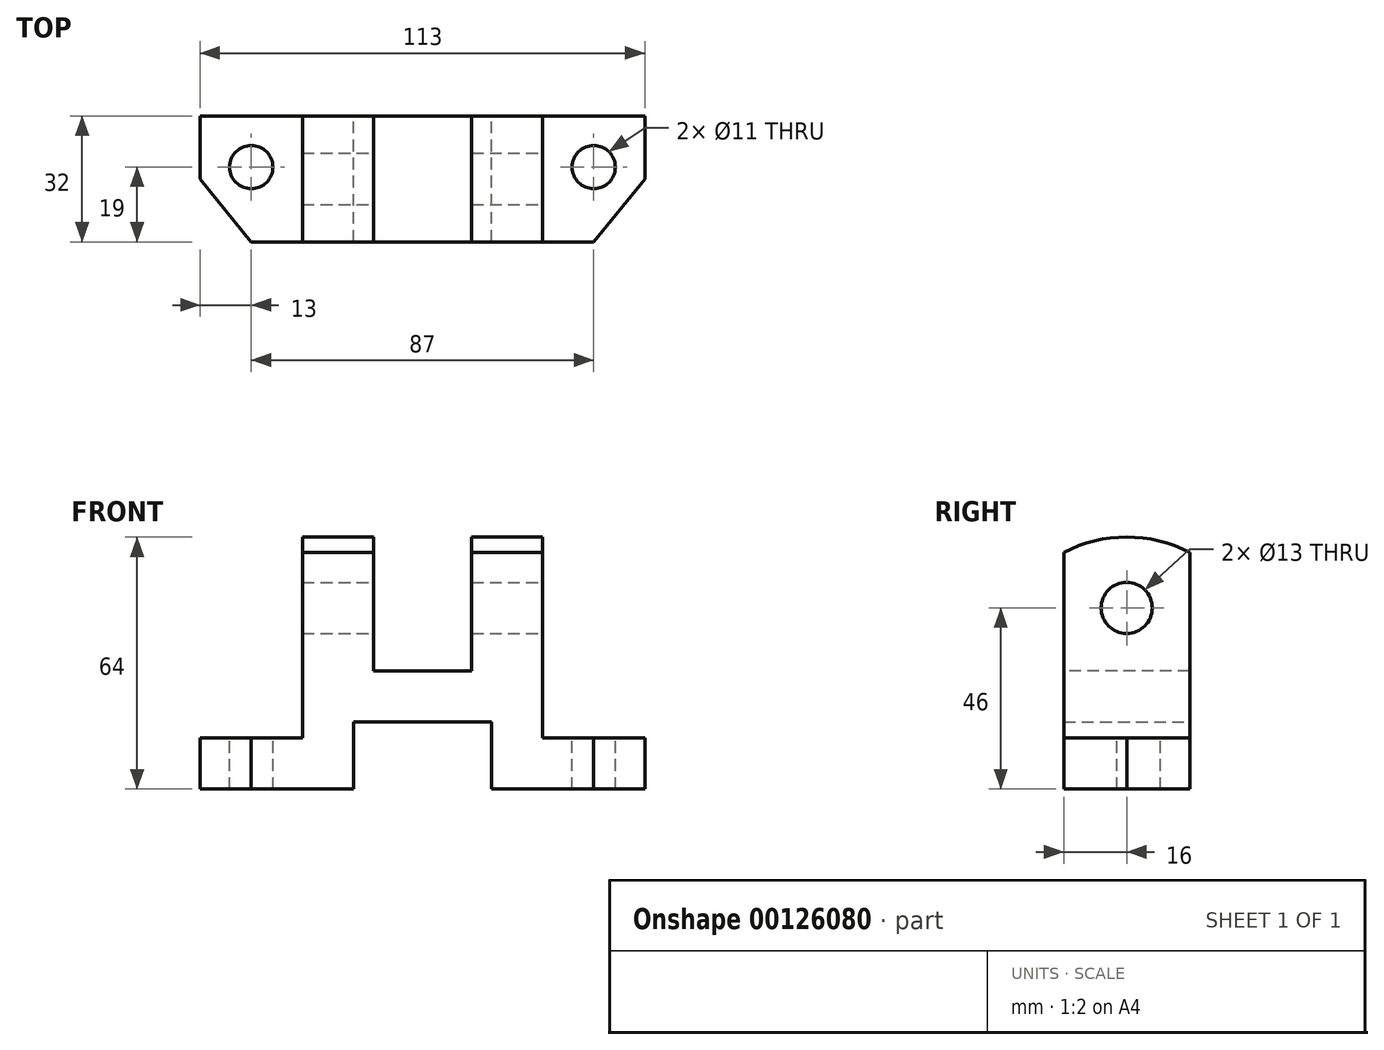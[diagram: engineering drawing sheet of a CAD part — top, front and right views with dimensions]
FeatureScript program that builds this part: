
annotation { "Feature Type Name" : "Feature", "Feature Type Description" : "" }
export const myFeature = defineFeature(function(context is Context, id is Id, definition is map)
    precondition{}
    {
        {
            var Q0;
            Q0=qCreatedBy(makeId("Right.planeOp"),FACE);
            var sketch = newSketch(context, id + "F0", { "sketchPlane" : qUnion([Q0])});
            skLineSegment(sketch, "E0.bottom", {"start": v(0, 0) * mm, "end": v(32, 0) * mm});
            skLineSegment(sketch, "E0.top", {"start": v(0, 13) * mm, "end": v(32, 13) * mm});
            skLineSegment(sketch, "E0.left", {"start": v(0, 0) * mm, "end": v(0, 13) * mm});
            skLineSegment(sketch, "E0.right", {"start": v(32, 0) * mm, "end": v(32, 13) * mm});
            skLineSegment(sketch, "E1", {"start": v(0, 13) * mm, "end": v(0, 60.13) * mm});
            skLineSegment(sketch, "E2", {"start": v(32, 13) * mm, "end": v(32, 60.13) * mm});
            skArc(sketch, "E3", {"start": v(32, 60.13) * mm, "mid": v(16, 64) * mm, "end": v(0, 60.13) * mm});
            skPoint(sketch, "E4", {"position": v(16, 64) * mm});
            skSolve(sketch);
        }
        {
            var Q0;
            Q0 = qSketchRegion(id + "F0", true);
            extrude(context, id + "F1", {"entities" : qUnion([Q0]), "depth" : 113 * mm});
        }
        {
            var Q0;
            Q0=makeQuery(id+"F1.opExtrude","SWEPT_FACE",FACE,{"disambiguationData":[OSD([sQuery(id+"F0.wireOp",EDGE,"E0.bottom")])]});
            var sketch = newSketch(context, id + "F2", { "sketchPlane" : qUnion([Q0])});
            skLineSegment(sketch, "E5.bottom", {"start": v(39, 0) * mm, "end": v(74, 0) * mm});
            skLineSegment(sketch, "E5.top", {"start": v(39, -32) * mm, "end": v(74, -32) * mm});
            skLineSegment(sketch, "E5.left", {"start": v(39, 0) * mm, "end": v(39, -32) * mm});
            skLineSegment(sketch, "E5.right", {"start": v(74, 0) * mm, "end": v(74, -32) * mm});
            skSolve(sketch);
        }
        {
            var Q0;
            Q0=makeQuery(id+"F2.imprint","IMPRINT",FACE,{"disambiguationData":[TD([[makeQuery(id+"F2.imprint","IMPRINT",EDGE,{"derivedFrom":sQuery(id+"F2.wireOp",EDGE,"E5.bottom")}),1.0]])]});
            extrude(context, id + "F3", {"entities" : qUnion([Q0]), "operationType" : NewBodyOperationType.REMOVE, "oppositeDirection" : true, "depth" : 17 * mm});
        }
        {
            var Q0;
            Q0=makeQuery(id+"F1.opExtrude","SWEPT_FACE",FACE,{"disambiguationData":[OSD([sQuery(id+"F0.wireOp",EDGE,"E0.left"),sQuery(id+"F0.wireOp",EDGE,"E1")])]});
            var sketch = newSketch(context, id + "F4", { "sketchPlane" : qUnion([Q0])});
            skLineSegment(sketch, "E6", {"start": v(113, 0) * mm, "end": v(113, 13) * mm});
            skLineSegment(sketch, "E7", {"start": v(113, 13) * mm, "end": v(87, 13) * mm});
            skLineSegment(sketch, "E8", {"start": v(87, 13) * mm, "end": v(87, 78.94) * mm});
            skLineSegment(sketch, "E9", {"start": v(87, 78.94) * mm, "end": v(74, 78.94) * mm});
            skLineSegment(sketch, "E10", {"start": v(69, 30) * mm, "end": v(44, 30) * mm});
            skLineSegment(sketch, "E11", {"start": v(44, 30) * mm, "end": v(44, 78.94) * mm});
            skLineSegment(sketch, "E12", {"start": v(44, 78.94) * mm, "end": v(26, 78.94) * mm});
            skLineSegment(sketch, "E13", {"start": v(26, 78.94) * mm, "end": v(26, 13) * mm});
            skLineSegment(sketch, "E14", {"start": v(0, 13) * mm, "end": v(0, 0) * mm});
            skLineSegment(sketch, "E15", {"start": v(44, 78.94) * mm, "end": v(74, 78.94) * mm});
            skLineSegment(sketch, "E16", {"start": v(87, 78.94) * mm, "end": v(113, 78.94) * mm});
            skLineSegment(sketch, "E17", {"start": v(113, 78.94) * mm, "end": v(113, 13) * mm});
            skLineSegment(sketch, "E18", {"start": v(26, 78.94) * mm, "end": v(0, 78.94) * mm});
            skLineSegment(sketch, "E19", {"start": v(0, 78.94) * mm, "end": v(0, 13) * mm});
            skPoint(sketch, "E20", {"position": v(56.5, 30) * mm});
            skPoint(sketch, "E21", {"position": v(56.5, 17) * mm});
            skLineSegment(sketch, "E22", {"start": v(56.5, 30) * mm, "end": v(56.5, 17) * mm, "construction": true});
            skLineSegment(sketch, "E23", {"start": v(26, 13) * mm, "end": v(0, 13) * mm});
            skLineSegment(sketch, "E24", {"start": v(69, 30) * mm, "end": v(69, 78.94) * mm});
            skSolve(sketch);
        }
        {
            var Q0;
            {var subQ0=sQuery(id+"F4.wireOp",EDGE,"E10");Q0=makeQuery(id+"F4.imprint","IMPRINT",FACE,{"disambiguationData":[TD([[makeQuery(id+"F4.imprint","IMPRINT",EDGE,{"derivedFrom":subQ0}),-1.0]])]});}
            var Q1;
            {var subQ0=sQuery(id+"F4.wireOp",EDGE,"E15");var subQ5=sQuery(id+"F4.wireOp",EDGE,"E24");var subQ6=makeQuery(id+"F4.imprint","INTERSECT",VERTEX,{"derivedFrom":[subQ0,subQ5]});Q1=makeQuery(id+"F4.imprint","IMPRINT",FACE,{"disambiguationData":[TD([[makeQuery(id+"F4.imprint","IMPRINT",EDGE,{"disambiguationData":[TD([[subQ6,1.0]])],"derivedFrom":subQ0}),-1.0]])]});}
            var Q2;
            {var subQ0=sQuery(id+"F4.wireOp",EDGE,"E7");Q2=makeQuery(id+"F4.imprint","IMPRINT",FACE,{"disambiguationData":[TD([[makeQuery(id+"F4.imprint","IMPRINT",EDGE,{"derivedFrom":subQ0}),-1.0]])]});}
            var Q3;
            {var subQ0=sQuery(id+"F4.wireOp",EDGE,"E16");Q3=makeQuery(id+"F4.imprint","IMPRINT",FACE,{"disambiguationData":[TD([[makeQuery(id+"F4.imprint","IMPRINT",EDGE,{"derivedFrom":subQ0}),-1.0]])]});}
            var Q4;
            {var subQ0=sQuery(id+"F4.wireOp",EDGE,"E18");Q4=makeQuery(id+"F4.imprint","IMPRINT",FACE,{"disambiguationData":[TD([[makeQuery(id+"F4.imprint","IMPRINT",EDGE,{"derivedFrom":subQ0}),1.0]])]});}
            var Q5;
            {var subQ0=sQuery(id+"F4.wireOp",EDGE,"E23");Q5=makeQuery(id+"F4.imprint","IMPRINT",FACE,{"disambiguationData":[TD([[makeQuery(id+"F4.imprint","IMPRINT",EDGE,{"derivedFrom":subQ0}),-1.0]])]});}
            extrude(context, id + "F5", {"entities" : qUnion([Q0, Q1, Q2, Q3, Q4, Q5]), "operationType" : NewBodyOperationType.REMOVE, "endBound" : BoundingType.THROUGH_ALL, "oppositeDirection" : true, "depth" : 25 * mm});
        }
        {
            var Q0;
            Q0=makeQuery(id+"F5.boolean.opBoolean","COPY",FACE,{"derivedFrom":makeQuery(id+"F5.opExtrude","SWEPT_FACE",FACE,{"disambiguationData":[OSD([sQuery(id+"F4.wireOp",EDGE,"E7")])]})});
            var sketch = newSketch(context, id + "F6", { "sketchPlane" : qUnion([Q0])});
            skLineSegment(sketch, "E25.bottom", {"start": v(87, 32) * mm, "end": v(113, 32) * mm});
            skLineSegment(sketch, "E25.top", {"start": v(87, 0) * mm, "end": v(100, 0) * mm});
            skLineSegment(sketch, "E25.left", {"start": v(87, 32) * mm, "end": v(87, 0) * mm});
            skLineSegment(sketch, "E25.right", {"start": v(113, 32) * mm, "end": v(113, 16) * mm});
            skLineSegment(sketch, "E26", {"start": v(100, 0) * mm, "end": v(113, 16) * mm});
            skCircle(sketch, "E27", {"center": v(100, 19) * mm, "radius": 5.5 * mm});
            skPoint(sketch, "E27.centerSnap0", {"position": v(100, 32) * mm});
            skSolve(sketch);
        }
        {
            var Q0;
            {var subQ0=sQuery(id+"F6.wireOp",EDGE,"E26");Q0=makeQuery(id+"F6.imprint","IMPRINT",FACE,{"disambiguationData":[TD([[makeQuery(id+"F6.imprint","IMPRINT",EDGE,{"derivedFrom":subQ0}),-1.0]])]});}
            var Q1;
            Q1=makeQuery(id+"F6.imprint","IMPRINT",FACE,{"disambiguationData":[TD([[makeQuery(id+"F6.imprint","IMPRINT",EDGE,{"derivedFrom":sQuery(id+"F6.wireOp",EDGE,"E27")}),1.0]])]});
            extrude(context, id + "F7", {"entities" : qUnion([Q0, Q1]), "operationType" : NewBodyOperationType.REMOVE, "endBound" : BoundingType.THROUGH_ALL, "oppositeDirection" : true, "depth" : 25 * mm});
        }
        {
            var Q0;
            Q0=makeQuery(id+"F5.boolean.opBoolean","COPY",FACE,{"derivedFrom":makeQuery(id+"F5.opExtrude","SWEPT_FACE",FACE,{"disambiguationData":[OSD([sQuery(id+"F4.wireOp",EDGE,"E23")])]})});
            var sketch = newSketch(context, id + "F8", { "sketchPlane" : qUnion([Q0])});
            skLineSegment(sketch, "E28.bottom", {"start": v(0, 0) * mm, "end": v(26, 0) * mm});
            skLineSegment(sketch, "E28.top", {"start": v(0, 32) * mm, "end": v(26, 32) * mm});
            skLineSegment(sketch, "E28.left", {"start": v(0, 0) * mm, "end": v(0, 32) * mm});
            skLineSegment(sketch, "E28.right", {"start": v(26, 0) * mm, "end": v(26, 32) * mm});
            skLineSegment(sketch, "E29", {"start": v(0, 16) * mm, "end": v(13, 0) * mm});
            skCircle(sketch, "E30", {"center": v(13, 19) * mm, "radius": 5.5 * mm});
            skPoint(sketch, "E30.centerSnap0", {"position": v(13, 32) * mm});
            skSolve(sketch);
        }
        {
            var Q0;
            Q0=makeQuery(id+"F8.imprint","IMPRINT",FACE,{"disambiguationData":[TD([[makeQuery(id+"F8.imprint","IMPRINT",EDGE,{"derivedFrom":sQuery(id+"F8.wireOp",EDGE,"E30")}),1.0]])]});
            var Q1;
            {var subQ3=sQuery(id+"F8.wireOp",EDGE,"E29");Q1=makeQuery(id+"F8.imprint","IMPRINT",FACE,{"disambiguationData":[TD([[makeQuery(id+"F8.imprint","IMPRINT",EDGE,{"derivedFrom":subQ3}),-1.0]])]});}
            extrude(context, id + "F9", {"entities" : qUnion([Q0, Q1]), "operationType" : NewBodyOperationType.REMOVE, "endBound" : BoundingType.THROUGH_ALL, "oppositeDirection" : true, "depth" : 25 * mm});
        }
        {
            var Q0;
            Q0=makeQuery(id+"F5.boolean.opBoolean","COPY",FACE,{"derivedFrom":makeQuery(id+"F5.opExtrude","SWEPT_FACE",FACE,{"disambiguationData":[OSD([sQuery(id+"F4.wireOp",EDGE,"E8")])]})});
            var sketch = newSketch(context, id + "F10", { "sketchPlane" : qUnion([Q0])});
            skCircle(sketch, "E31", {"center": v(16, 46) * mm, "radius": 6.5 * mm});
            skPoint(sketch, "E31.centerSnap0", {"position": v(16, 64) * mm});
            skSolve(sketch);
        }
        {
            var Q0;
            Q0=makeQuery(id+"F10.imprint","IMPRINT",FACE,{"disambiguationData":[TD([[makeQuery(id+"F10.imprint","IMPRINT",EDGE,{"derivedFrom":sQuery(id+"F10.wireOp",EDGE,"E31")}),1.0]])]});
            extrude(context, id + "F11", {"entities" : qUnion([Q0]), "operationType" : NewBodyOperationType.REMOVE, "endBound" : BoundingType.THROUGH_ALL, "oppositeDirection" : true, "depth" : 25 * mm});
        }
    });
